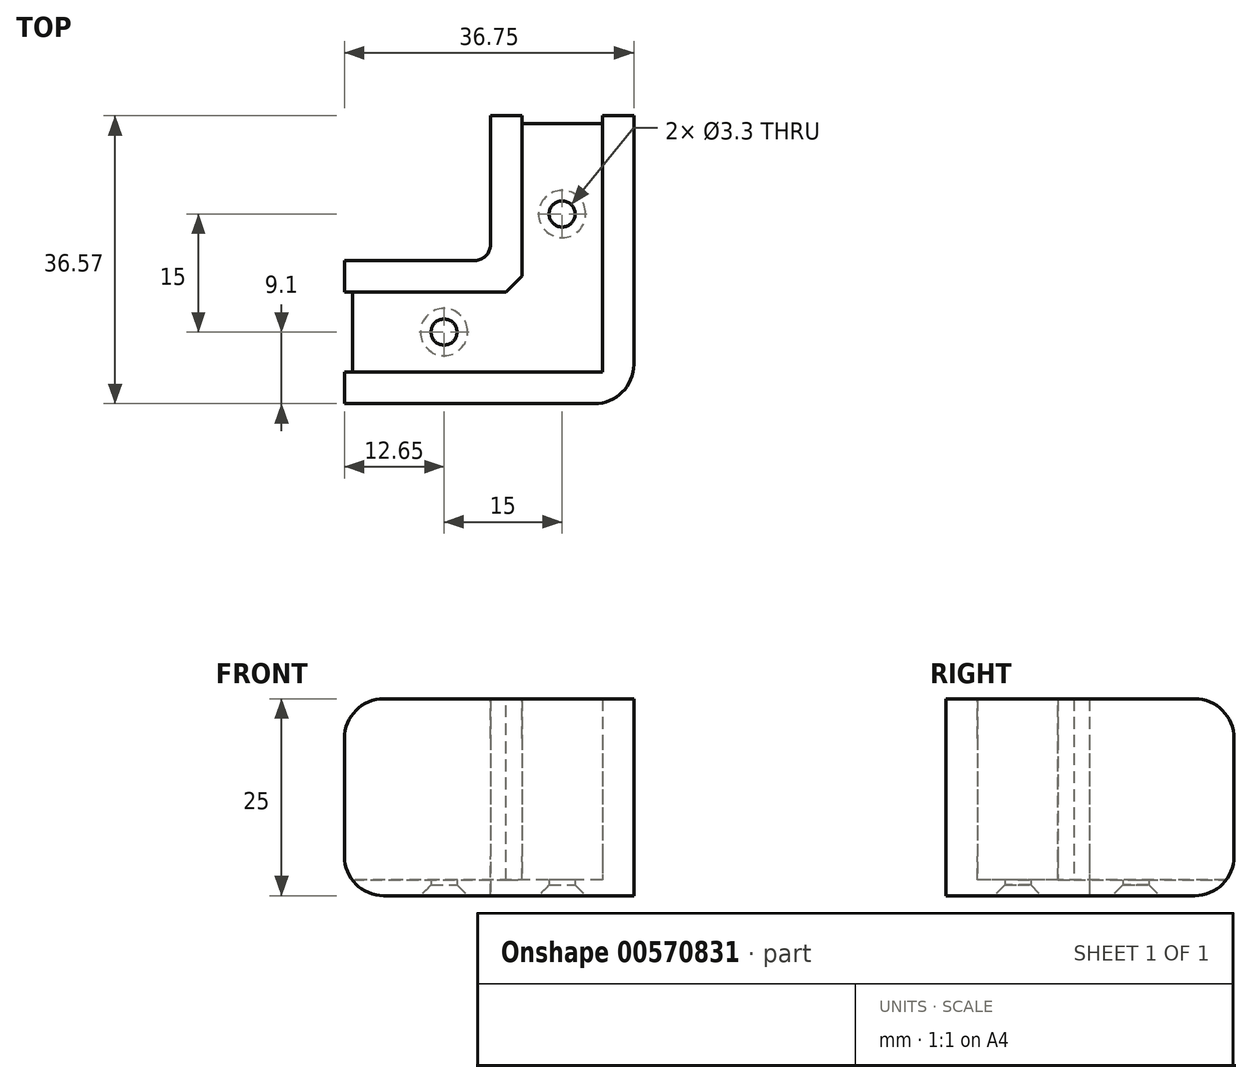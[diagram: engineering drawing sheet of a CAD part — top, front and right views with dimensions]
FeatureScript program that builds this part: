
annotation { "Feature Type Name" : "Feature", "Feature Type Description" : "" }
export const myFeature = defineFeature(function(context is Context, id is Id, definition is map)
    precondition{}
    {
        {
            var Q0;
            Q0=qCreatedBy(makeId("Top.planeOp"),FACE);
            var sketch = newSketch(context, id + "F0", { "sketchPlane" : qUnion([Q0])});
            skLineSegment(sketch, "E0", {"start": v(5.1, 10.2) * mm, "end": v(5.1, 32.57) * mm});
            skLineSegment(sketch, "E1", {"start": v(-5.1, 32.57) * mm, "end": v(-5.1, 10.2) * mm});
            skLineSegment(sketch, "E2", {"start": v(-5.1, 10.2) * mm, "end": v(-27.65, 10.2) * mm});
            skLineSegment(sketch, "E3", {"start": v(-27.65, 0) * mm, "end": v(0, 0) * mm});
            skLineSegment(sketch, "E4.0", {"start": v(9.1, 32.57) * mm, "end": v(-9.1, 32.57) * mm});
            skLineSegment(sketch, "E4.2", {"start": v(-9.1, 32.57) * mm, "end": v(-9.1, 14.2) * mm});
            skLineSegment(sketch, "E4.5", {"start": v(-9.1, 14.2) * mm, "end": v(-27.65, 14.2) * mm});
            skLineSegment(sketch, "E4.6", {"start": v(-27.65, 14.2) * mm, "end": v(-27.65, -4) * mm});
            skLineSegment(sketch, "E4.7", {"start": v(-27.65, -4) * mm, "end": v(0, -4) * mm});
            skLineSegment(sketch, "E5", {"start": v(9.1, 32.57) * mm, "end": v(9.1, -4) * mm});
            skLineSegment(sketch, "E6", {"start": v(0, -4) * mm, "end": v(9.1, -4) * mm});
            skLineSegment(sketch, "E7", {"start": v(0, 0) * mm, "end": v(5.1, 0) * mm});
            skLineSegment(sketch, "E8", {"start": v(5.1, 0) * mm, "end": v(5.1, 10.2) * mm});
            skPoint(sketch, "E9", {"position": v(0, 32.57) * mm});
            skSolve(sketch);
        }
        {
            var Q0;
            Q0=qSketchRegion(id+"F0",true);
            extrude(context, id + "F1", {"entities" : qUnion([Q0]), "depth" : 2 * mm, "offsetDistance" : 25 * mm});
        }
        {
            var Q0;
            {var subQ3=sQuery(id+"F0.wireOp",EDGE,"E1");Q0=makeQuery(id+"F0.imprint","IMPRINT",FACE,{"disambiguationData":[TD([[makeQuery(id+"F0.imprint","IMPRINT",EDGE,{"derivedFrom":subQ3}),-1.0]])]});}
            var Q1;
            {var subQ3=sQuery(id+"F0.wireOp",EDGE,"E0");Q1=makeQuery(id+"F0.imprint","IMPRINT",FACE,{"disambiguationData":[TD([[makeQuery(id+"F0.imprint","IMPRINT",EDGE,{"derivedFrom":subQ3}),-1.0]])]});}
            extrude(context, id + "F2", {"entities" : qUnion([Q0, Q1]), "operationType" : NewBodyOperationType.ADD, "depth" : 25 * mm, "offsetDistance" : 25 * mm});
        }
        {
            var Q0;
            {var subQ0=sQuery(id+"F0.wireOp",EDGE,"E4.4");Q0=makeQuery(id+"F2.opExtrude","CAP_EDGE",EDGE,{"disambiguationData":[OSD([subQ0]),TDD([makeQuery(id+"F0.imprint","IMPRINT",EDGE,{"disambiguationData":[TD([[makeQuery(id+"F0.imprint","INTERSECT",VERTEX,{"derivedFrom":[sQuery(id+"F0.wireOp",EDGE,"4AKFVKuP-VGzW-Z0gR-biP7-avwRZvC0l9sY"),subQ0]}),1.0]])],"derivedFrom":subQ0})])],"isStart":false});}
            var Q1;
            {var subQ0=sQuery(id+"F0.wireOp",EDGE,"E4.4");Q1=makeQuery(id+"F2.opExtrude","CAP_EDGE",EDGE,{"disambiguationData":[OSD([subQ0]),TDD([makeQuery(id+"F0.imprint","IMPRINT",EDGE,{"disambiguationData":[TD([[makeQuery(id+"F0.imprint","INTERSECT",VERTEX,{"derivedFrom":[sQuery(id+"F0.wireOp",EDGE,"wGMG52vS-Bb6S-6M2K-uLHt-X8AWWQIAXK16"),subQ0]}),-1.0]])],"derivedFrom":subQ0})])],"isStart":false});}
            var Q2;
            {var subQ0=sQuery(id+"F0.wireOp",EDGE,"E4.6");Q2=makeQuery(id+"F2.opExtrude","CAP_EDGE",EDGE,{"disambiguationData":[OSD([subQ0]),TDD([makeQuery(id+"F0.imprint","IMPRINT",EDGE,{"disambiguationData":[TD([[makeQuery(id+"F0.imprint","INTERSECT",VERTEX,{"derivedFrom":[sQuery(id+"F0.wireOp",EDGE,"E3"),subQ0]}),-1.0]])],"derivedFrom":subQ0})])],"isStart":false});}
            var Q3;
            {var subQ0=sQuery(id+"F0.wireOp",EDGE,"E4.6");Q3=makeQuery(id+"F2.opExtrude","CAP_EDGE",EDGE,{"disambiguationData":[OSD([subQ0]),TDD([makeQuery(id+"F0.imprint","IMPRINT",EDGE,{"disambiguationData":[TD([[makeQuery(id+"F0.imprint","INTERSECT",VERTEX,{"derivedFrom":[sQuery(id+"F0.wireOp",EDGE,"E2"),subQ0]}),1.0]])],"derivedFrom":subQ0})])],"isStart":false});}
            var Q4;
            {var subQ0=sQuery(id+"F0.wireOp",EDGE,"E4.0");Q4=makeQuery(id+"F2.opExtrude","CAP_EDGE",EDGE,{"disambiguationData":[OSD([subQ0]),TDD([makeQuery(id+"F0.imprint","IMPRINT",EDGE,{"disambiguationData":[TD([[makeQuery(id+"F0.imprint","INTERSECT",VERTEX,{"derivedFrom":[sQuery(id+"F0.wireOp",EDGE,"E1"),subQ0]}),-1.0]])],"derivedFrom":subQ0})])],"isStart":false});}
            var Q5;
            {var subQ0=sQuery(id+"F0.wireOp",EDGE,"E4.0");Q5=makeQuery(id+"F2.opExtrude","CAP_EDGE",EDGE,{"disambiguationData":[OSD([subQ0]),TDD([makeQuery(id+"F0.imprint","IMPRINT",EDGE,{"disambiguationData":[TD([[makeQuery(id+"F0.imprint","INTERSECT",VERTEX,{"derivedFrom":[sQuery(id+"F0.wireOp",EDGE,"E0"),subQ0]}),1.0]])],"derivedFrom":subQ0})])],"isStart":false});}
            var Q6;
            Q6=makeQuery(id+"F1.opExtrude","CAP_EDGE",EDGE,{"disambiguationData":[OSD([sQuery(id+"F0.wireOp",EDGE,"E4.6")])],"isStart":true});
            var Q7;
            Q7=makeQuery(id+"F1.opExtrude","CAP_EDGE",EDGE,{"disambiguationData":[OSD([sQuery(id+"F0.wireOp",EDGE,"E4.4")])],"isStart":true});
            var Q8;
            Q8=makeQuery(id+"F1.opExtrude","CAP_EDGE",EDGE,{"disambiguationData":[OSD([sQuery(id+"F0.wireOp",EDGE,"E4.0")])],"isStart":true});
            var Q9;
            {var subQ0=sQuery(id+"F0.wireOp",EDGE,"E6");var subQ1=sQuery(id+"F0.wireOp",EDGE,"E5");Q9=makeQuery(id+"F2.boolean.opBoolean","MERGE",EDGE,{"derivedFrom":[makeQuery(id+"F1.opExtrude","SWEPT_EDGE",EDGE,{"disambiguationData":[OSD([subQ1,subQ0])]}),makeQuery(id+"F2.opExtrude","SWEPT_EDGE",EDGE,{"disambiguationData":[OSD([subQ1,subQ0])]})]});}
            fillet(context, id + "F3", {"entities" : qUnion([Q0, Q1, Q2, Q3, Q4, Q5, Q6, Q7, Q8, Q9]), "radius" : 5 * mm, "tangentPropagation" : true, "allowEdgeOverflow" : false});
        }
        {
            var Q0;
            {var subQ0=sQuery(id+"F0.wireOp",EDGE,"E4.5");var subQ1=sQuery(id+"F0.wireOp",EDGE,"E4.2");Q0=makeQuery(id+"F2.boolean.opBoolean","MERGE",EDGE,{"derivedFrom":[makeQuery(id+"F1.opExtrude","SWEPT_EDGE",EDGE,{"disambiguationData":[OSD([subQ1,subQ0])]}),makeQuery(id+"F2.opExtrude","SWEPT_EDGE",EDGE,{"disambiguationData":[OSD([subQ1,subQ0])]})]});}
            fillet(context, id + "F4", {"entities" : qUnion([Q0]), "radius" : 2 * mm, "tangentPropagation" : true, "allowEdgeOverflow" : false});
        }
        {
            var Q0;
            Q0=makeQuery(id+"F2.opExtrude","SWEPT_EDGE",EDGE,{"disambiguationData":[OSD([sQuery(id+"F0.wireOp",EDGE,"E1"),sQuery(id+"F0.wireOp",EDGE,"E2")])]});
            chamfer(context, id + "F5", {"entities" : qUnion([Q0]), "width" : 2 * mm, "tangentPropagation" : true});
        }
        {
            var Q0;
            {var subQ3=sQuery(id+"F0.wireOp",EDGE,"E0");Q0=makeQuery(id+"F0.imprint","IMPRINT",FACE,{"disambiguationData":[TD([[makeQuery(id+"F0.imprint","IMPRINT",EDGE,{"derivedFrom":subQ3}),1.0]])]});}
            var sketch = newSketch(context, id + "F6", { "sketchPlane" : qUnion([Q0])});
            skLineSegment(sketch, "E10", {"start": v(-22.65, 5.1) * mm, "end": v(7.14, 5.1) * mm});
            skPoint(sketch, "E11", {"position": v(-15, 5.1) * mm});
            skPoint(sketch, "E12", {"position": v(0, 20.1) * mm});
            skSolve(sketch);
        }
        {
            var Q0;
            Q0=sQuery(id+"F6.wireOp",VERTEX,"E11");
            var Q1;
            Q1=sQuery(id+"F6.wireOp",VERTEX,"E12");
            var Q2;
            Q2=sQuery(id+"F6.wireOp",VERTEX,"148682fb-4106-4836-a6ce-08a78baf88f0");
            var Q3;
            Q3=makeQuery(id+"F1.opExtrude","SWEPT_BODY",BODY,{"disambiguationData":[OSD([sQuery(id+"F0.wireOp",EDGE,"E4.0"),sQuery(id+"F0.wireOp",EDGE,"E4.1"),sQuery(id+"F0.wireOp",EDGE,"E4.2"),sQuery(id+"F0.wireOp",EDGE,"E4.3"),sQuery(id+"F0.wireOp",EDGE,"E4.4"),sQuery(id+"F0.wireOp",EDGE,"E4.5"),sQuery(id+"F0.wireOp",EDGE,"E4.6"),sQuery(id+"F0.wireOp",EDGE,"E4.7"),sQuery(id+"F0.wireOp",EDGE,"E4.8")])]});
            hole(context, id + "F7", {"style" : HoleStyle.C_SINK, "endStyle" : HoleEndStyle.THROUGH, "oppositeDirection" : true, "holeDiameter" : 3.3 * mm, "cSinkDiameter" : 6 * mm, "cSinkAngle" : 90 * degree, "majorDiameter" : 5 * mm, "isTappedThrough" : true, "tappedDepth" : 12 * mm, "tapClearance" : 3, "locations" : qUnion([Q0, Q1, Q2]), "scope" : qUnion([Q3])});
        }
    });
